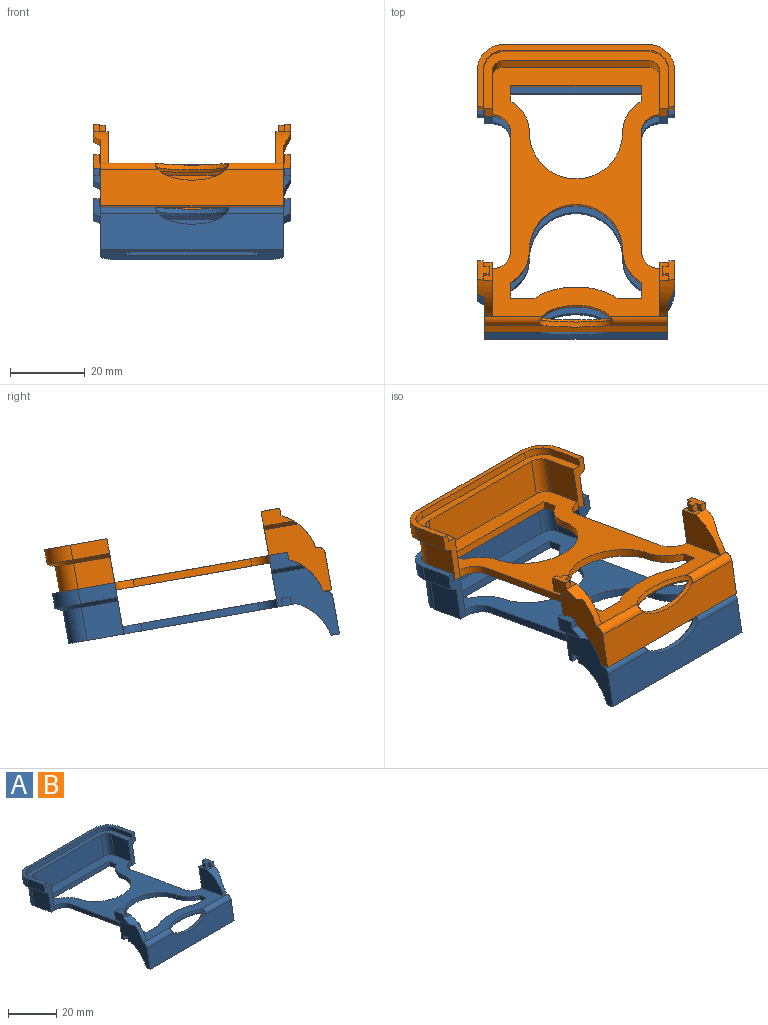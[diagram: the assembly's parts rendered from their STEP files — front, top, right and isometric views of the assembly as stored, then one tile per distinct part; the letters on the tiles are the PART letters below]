
ASSEMBLY  parts=2 mates=1
PART A: 100 faces, bbox 53.2x77.2x24.8 mm
  f0: plane 17.72x16.39mm, normal (1,0,0), area 132.3mm2, adj f1,f3,f66,f67,f68,f69,f94,f95
  f1: plane 1.97x1.4mm, normal (0,0.98,-0.17), area 2.8mm2, adj f0,f2,f97,f99
  f2: plane 2.71x2.39mm, normal (1,0,0), area 4.8mm2, adj f1,f97,f98,f99
  f3: cylinder r=14.13mm len=9.28mm, axis (1,0,0), area 26.1mm2, adj f0,f4,f66,f97
  f4: plane 9.89x9.54mm, normal (-1,0,0), area 28.3mm2, adj f3,f5,f66,f97
  f5: plane 45.17x10.01mm, normal (0,0.98,-0.17), area 404.4mm2, adj f4,f6,f9,f66,f97
  f6: bspline ~20.24x5.01mm, area 17.5mm2, adj f5,f7,f8
  f7: revolved ~18.7x4.34mm, area 73.7mm2, adj f6,f8
  f8: bspline ~20.24x4.81mm, area 17.5mm2, adj f6,f7,f97
  f9: plane 9.89x9.54mm, normal (1,0,0), area 28.3mm2, adj f5,f10,f66,f97
  f10: cylinder r=14.13mm len=9.28mm, axis (-1,0,0), area 26.1mm2, adj f9,f11,f66,f97
  f11: plane 18.09x18.07mm, normal (-1,0,0), area 152.2mm2, adj f10,f12,f58,f59,f60,f62,f64,f65
  f12: plane 13.79x4mm, normal (0,0.98,-0.17), area 32.2mm2, adj f11,f13,f19,f20,f21,f22,f57,f58
  f13: plane 5x2.4mm, normal (0,0.17,0.98), area 9mm2, adj f12,f14,f16,f17,f18,f19,f57,f59
  f14: plane 2.24x1.9mm, normal (1,0,0), area 3.2mm2, adj f13,f15,f16,f20
  f15: plane 1.97x1.6mm, normal (0,-0.98,0.17), area 3.2mm2, adj f14,f20,f21,f59
  f16: plane 1.97x1.6mm, normal (0,-0.98,0.17), area 3.2mm2, adj f13,f14,f17,f20
  f17: plane 2.32x2.32mm, normal (1,0,0), area 4mm2, adj f13,f16,f18,f20
  f18: plane 1.97x1.6mm, normal (0,0.98,-0.17), area 3.2mm2, adj f13,f17,f19,f20
  f19: plane 2.23x1.82mm, normal (1,0,0), area 3mm2, adj f12,f13,f18,f20
  f20: plane 5x3.2mm, normal (0,0.17,0.98), area 11.3mm2, adj f12,f14,f15,f16,f17,f18,f19,f21
  f21: plane 8.68x4.82mm, normal (-1,0,0), area 23.6mm2, adj f12,f15,f20,f58,f59
  f22: cylinder r=5mm len=5.27mm, axis (0,0.17,0.98), area 15.7mm2, adj f12,f23,f69,f97
  f23: plane 31.86x7.53mm, normal (-1,0,0), area 64mm2, adj f22,f24,f69,f97
  f24: cylinder r=5mm len=5.27mm, axis (0,-0.17,-0.98), area 15.7mm2, adj f23,f25,f69,f97
  f25: plane 13.79x4mm, normal (0,-0.98,0.17), area 32.2mm2, adj f24,f26,f51,f52,f53,f54,f55,f56
  f26: plane 11.41x10.6mm, normal (-1,0,0), area 90mm2, adj f25,f27,f51,f97
  f27: cylinder r=5mm len=9.73mm, axis (0,-0.17,-0.98), area 70.7mm2, adj f26,f28,f50,f97
  f28: plane 39x8.86mm, normal (0,0.98,-0.17), area 351mm2, adj f27,f29,f49,f97
  f29: cylinder r=5mm len=9.73mm, axis (0,0.17,0.98), area 70.7mm2, adj f28,f30,f48,f97
  f30: plane 11.41x10.6mm, normal (1,0,0), area 90mm2, adj f29,f31,f47,f97
  f31: plane 13.79x4mm, normal (0,-0.98,0.17), area 32.2mm2, adj f30,f32,f36,f40,f43,f47,f53,f55
  f32: plane 10.2x3.71mm, normal (-1,0,0), area 20mm2, adj f31,f33,f53,f55
  f33: cylinder r=5.4mm len=5.67mm, axis (0,-0.17,-0.98), area 17mm2, adj f32,f34,f53,f55
  f34: plane 39x1.97mm, normal (0,-0.98,0.17), area 78mm2, adj f33,f35,f53,f55
  f35: cylinder r=5.4mm len=5.67mm, axis (0,-0.17,-0.98), area 17mm2, adj f34,f53,f54,f55
  f36: plane 10.54x5.68mm, normal (1,0,0), area 40mm2, adj f31,f37,f47,f53
  f37: cylinder r=7mm len=7.59mm, axis (0,-0.17,-0.98), area 44mm2, adj f36,f38,f48,f53
  f38: plane 39x3.94mm, normal (0,0.98,-0.17), area 156mm2, adj f37,f39,f49,f53
  f39: cylinder r=7mm len=7.59mm, axis (0,-0.17,-0.98), area 44mm2, adj f38,f50,f52,f53
  f40: cylinder r=5mm len=5.27mm, axis (0,0.17,0.98), area 15.7mm2, adj f31,f41,f69,f97
  f41: plane 31.86x7.53mm, normal (1,0,0), area 64mm2, adj f40,f42,f69,f97
  f42: cylinder r=5mm len=5.27mm, axis (0,-0.17,-0.98), area 15.7mm2, adj f41,f69,f96,f97
  f43: plane 11.58x11.58mm, normal (-1,0,0), area 100mm2, adj f31,f44,f55,f69
  f44: cylinder r=3mm len=10.37mm, axis (0,-0.17,-0.98), area 47.1mm2, adj f43,f45,f55,f69
  f45: plane 39x9.85mm, normal (0,-0.98,0.17), area 390mm2, adj f44,f46,f55,f69
  f46: cylinder r=3mm len=10.37mm, axis (0,0.17,0.98), area 47.1mm2, adj f45,f55,f56,f69
  f47: plane 10.02x2.72mm, normal (0.45,-0.16,-0.88), area 22.4mm2, adj f30,f31,f36,f48
  f48: cone r=9mm half-angle=63.4deg, axis (0,0.17,0.98), area 21.1mm2, adj f29,f37,f47,f49
  f49: plane 39x2.14mm, normal (0,0.29,-0.96), area 87.2mm2, adj f28,f38,f48,f50
  f50: cone r=9mm half-angle=63.4deg, axis (0,0.17,0.98), area 21.1mm2, adj f27,f39,f49,f51
  f51: plane 10.02x2.72mm, normal (-0.45,-0.16,-0.88), area 22.4mm2, adj f25,f26,f50,f52
  f52: plane 10.54x5.68mm, normal (-1,0,0), area 40mm2, adj f25,f39,f51,f53
  f53: plane 53x16.74mm, normal (0,0.17,0.98), area 125.6mm2, adj f25,f31,f32,f33,f34,f35,f36,f37
  f54: plane 10.2x3.71mm, normal (1,0,0), area 20mm2, adj f25,f35,f53,f55
  f55: plane 49.8x15.17mm, normal (0,0.17,0.98), area 173.3mm2, adj f25,f31,f32,f33,f34,f35,f43,f44
  f56: plane 11.58x11.58mm, normal (1,0,0), area 100mm2, adj f25,f46,f55,f69
  f57: plane 14.28x10.73mm, normal (1,0,0), area 101.7mm2, adj f12,f13,f59,f69
  f58: plane 9.24x2.45mm, normal (-0.45,-0.16,-0.88), area 19.3mm2, adj f11,f12,f21,f59
  f59: cylinder r=14.13mm len=9.28mm, axis (-1,0,0), area 34.8mm2, adj f11,f13,f15,f21,f57,f58,f69
  f60: cylinder r=2mm len=15.34mm, axis (1,0,0), area 46.9mm2, adj f11,f61,f67,f69
  f61: revolved ~18.33x5.79mm, area 126.9mm2, adj f60,f67,f68,f69
  f62: plane 1.97x1.4mm, normal (0,0.98,-0.17), area 2.8mm2, adj f11,f63,f64,f97
  f63: plane 2.71x2.39mm, normal (-1,0,0), area 4.8mm2, adj f62,f64,f65,f97
  f64: plane 2.36x1.4mm, normal (0,-0.17,-0.98), area 3.4mm2, adj f11,f62,f63,f65
  f65: plane 1.97x1.4mm, normal (0,-0.98,0.17), area 2.8mm2, adj f11,f63,f64,f97
  f66: plane 49x2.23mm, normal (0,-0.17,-0.98), area 99mm2, adj f0,f3,f4,f5,f9,f10,f11,f67
  f67: plane 49x9.85mm, normal (0,-0.98,0.17), area 450.4mm2, adj f0,f11,f60,f61,f66,f68
  f68: cylinder r=2mm len=15.34mm, axis (1,0,0), area 46.9mm2, adj f0,f61,f67,f69
  f69: plane 66.97x49mm, normal (0,0.17,0.98), area 1386.9mm2, adj f0,f11,f22,f23,f24,f40,f41,f42
  f70: plane 14.28x10.73mm, normal (-1,0,0), area 101.7mm2, adj f69,f71,f94,f96
  f71: plane 5x2.4mm, normal (0,0.17,0.98), area 9mm2, adj f70,f72,f76,f77,f78,f79,f94,f96
  f72: plane 2.32x2.32mm, normal (-1,0,0), area 4mm2, adj f71,f73,f76,f79
  f73: plane 5x3.2mm, normal (0,0.17,0.98), area 11.3mm2, adj f72,f74,f75,f76,f77,f78,f79,f96
  f74: plane 7.22x3.84mm, normal (1,0,0), area 16.1mm2, adj f73,f75,f94,f95,f96
  f75: plane 1.97x1.6mm, normal (0,-0.98,0.17), area 3.2mm2, adj f73,f74,f77,f94
  f76: plane 1.97x1.6mm, normal (0,-0.98,0.17), area 3.2mm2, adj f71,f72,f73,f77
  f77: plane 2.24x1.9mm, normal (-1,0,0), area 3.2mm2, adj f71,f73,f75,f76
  f78: plane 2.23x1.82mm, normal (-1,0,0), area 3mm2, adj f71,f73,f79,f96
  f79: plane 1.97x1.6mm, normal (0,0.98,-0.17), area 3.2mm2, adj f71,f72,f73,f78
  f80: cylinder r=10mm len=8.88mm, axis (0,0.17,0.98), area 20.9mm2, adj f69,f81,f85,f97
  f81: extruded ~25x12.66mm, area 78.5mm2, adj f69,f80,f82,f97
  f82: cylinder r=10mm len=8.88mm, axis (0,0.17,0.98), area 20.9mm2, adj f69,f81,f83,f97
  f83: plane 4.62x2.72mm, normal (-1,0,0), area 8.7mm2, adj f69,f82,f84,f97
  f84: plane 35x1.97mm, normal (0,-0.98,0.17), area 70mm2, adj f69,f83,f85,f97
  f85: plane 4.62x2.72mm, normal (1,0,0), area 8.7mm2, adj f69,f80,f84,f97
  f86: cylinder r=10mm len=8.88mm, axis (0,0.17,0.98), area 20.9mm2, adj f69,f87,f93,f97
  f87: plane 4.62x2.72mm, normal (1,0,0), area 8.7mm2, adj f69,f86,f88,f97
  f88: plane 6.49x1.97mm, normal (0,0.98,-0.17), area 13mm2, adj f69,f87,f89,f97
  f89: extruded ~22.02x3.3mm, area 46.3mm2, adj f69,f88,f90,f97
  f90: plane 6.49x1.97mm, normal (0,0.98,-0.17), area 13mm2, adj f69,f89,f91,f97
  f91: plane 4.62x2.72mm, normal (-1,0,0), area 8.7mm2, adj f69,f90,f92,f97
  f92: cylinder r=10mm len=8.88mm, axis (0,0.17,0.98), area 20.9mm2, adj f69,f91,f93,f97
  f93: extruded ~25x12.66mm, area 78.5mm2, adj f69,f86,f92,f97
  f94: cylinder r=14.13mm len=9.28mm, axis (1,0,0), area 35.7mm2, adj f0,f69,f70,f71,f74,f75,f95
  f95: plane 11.45x5.32mm, normal (0.89,-0.08,-0.44), area 40.4mm2, adj f0,f74,f94,f96
  f96: plane 13.79x4mm, normal (0,0.98,-0.17), area 33.2mm2, adj f0,f42,f70,f71,f73,f74,f78,f95
  f97: plane 69.1x49.17mm, normal (0,-0.17,-0.98), area 1536.4mm2, adj f0,f1,f2,f3,f4,f5,f8,f9
  f98: plane 1.97x1.4mm, normal (0,-0.98,0.17), area 2.8mm2, adj f0,f2,f97,f99
  f99: plane 2.36x1.4mm, normal (0,-0.17,-0.98), area 3.4mm2, adj f0,f1,f2,f98
PART B: same geometry as A
PLACE A t=(31.97,-25.03,-17.77)mm
PLACE B t=(31.97,-22.95,-5.95)mm
MATE fastened B.f27 <-> A.f27  axis (0,-0.17,-0.98) through (12.47,7.35,-18.4)mm
